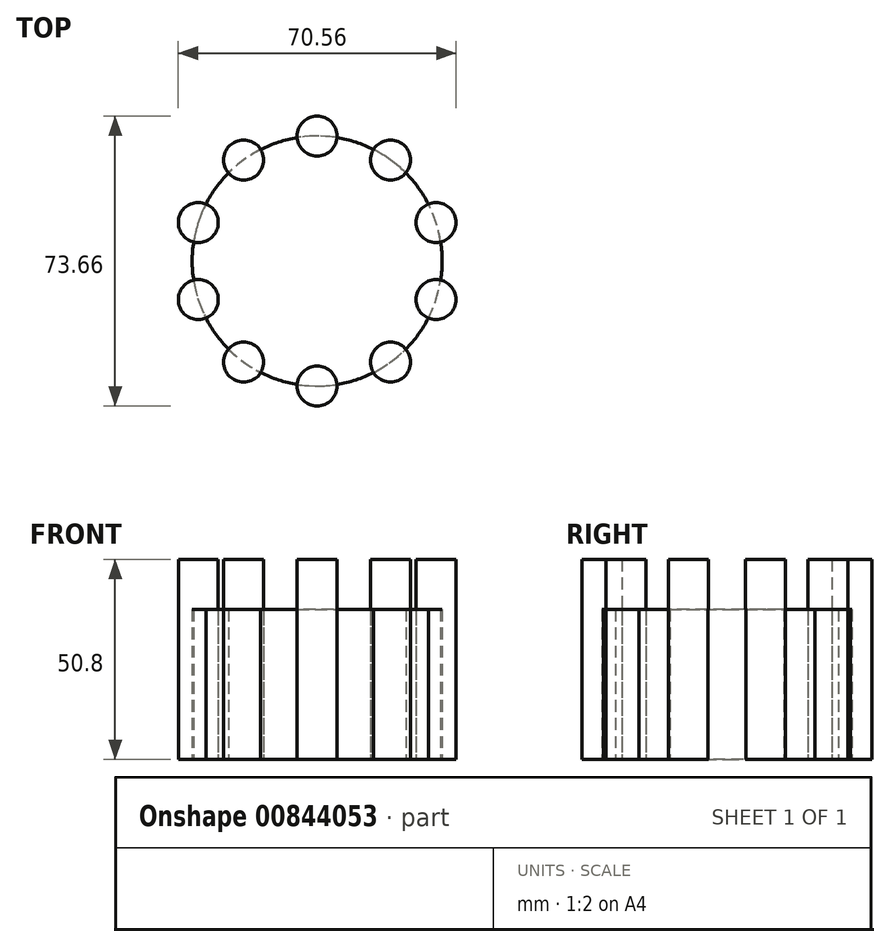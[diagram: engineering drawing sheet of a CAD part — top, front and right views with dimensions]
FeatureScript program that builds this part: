
annotation { "Feature Type Name" : "Feature", "Feature Type Description" : "" }
export const myFeature = defineFeature(function(context is Context, id is Id, definition is map)
    precondition{}
    {
        {
            var Q0;
            Q0=qCreatedBy(makeId("Top.planeOp"),FACE);
            var sketch = newSketch(context, id + "F0", { "sketchPlane" : qUnion([Q0])});
            skCircle(sketch, "E0", {"center": v(0, 0) * mm, "radius": 31.75 * mm});
            skSolve(sketch);
        }
        {
            var Q0;
            Q0=qSketchRegion(id+"F0",true);
            extrude(context, id + "F1", {"entities" : qUnion([Q0]), "depth" : 38.1 * mm});
        }
        {
            var Q0;
            Q0=qCreatedBy(makeId("Top.planeOp"),FACE);
            var sketch = newSketch(context, id + "F2", { "sketchPlane" : qUnion([Q0])});
            skCircle(sketch, "E1", {"center": v(0, 31.75) * mm, "radius": 5.08 * mm});
            skCircle(sketch, "E2.1.0", {"center": v(-18.66, 25.69) * mm, "radius": 5.08 * mm});
            skCircle(sketch, "E2.2.0", {"center": v(-30.2, 9.81) * mm, "radius": 5.08 * mm});
            skCircle(sketch, "E2.3.0", {"center": v(-30.2, -9.81) * mm, "radius": 5.08 * mm});
            skCircle(sketch, "E2.4.0", {"center": v(-18.66, -25.69) * mm, "radius": 5.08 * mm});
            skCircle(sketch, "E2.5.0", {"center": v(0, -31.75) * mm, "radius": 5.08 * mm});
            skCircle(sketch, "E2.6.0", {"center": v(18.66, -25.69) * mm, "radius": 5.08 * mm});
            skCircle(sketch, "E2.7.0", {"center": v(30.2, -9.81) * mm, "radius": 5.08 * mm});
            skCircle(sketch, "E2.8.0", {"center": v(30.2, 9.81) * mm, "radius": 5.08 * mm});
            skCircle(sketch, "E2.9.0", {"center": v(18.66, 25.69) * mm, "radius": 5.08 * mm});
            skPoint(sketch, "E2.center", {"position": v(0, 0) * mm});
            skSolve(sketch);
        }
        {
            var Q0;
            Q0=qSketchRegion(id+"F2",true);
            extrude(context, id + "F3", {"entities" : qUnion([Q0]), "depth" : 50.8 * mm});
        }
        {
            var Q0;
            Q0=makeQuery(id+"F3.opExtrude","SWEPT_BODY",BODY,{"disambiguationData":[OSD([sQuery(id+"F2.wireOp",EDGE,"E2.4.0")])]});
            var Q1;
            Q1=makeQuery(id+"F1.opExtrude","SWEPT_BODY",BODY,{"disambiguationData":[OSD([sQuery(id+"F0.wireOp",EDGE,"E0")])]});
            booleanBodies(context, id + "F4", {"operationType" : BooleanOperationType.INTERSECTION, "tools" : qUnion([Q0, Q1]), "keepTools" : true});
        }
        {
            var Q0;
            Q0=makeQuery(id+"F3.opExtrude","SWEPT_BODY",BODY,{"disambiguationData":[OSD([sQuery(id+"F2.wireOp",EDGE,"E2.3.0")])]});
            var Q1;
            Q1=makeQuery(id+"F1.opExtrude","SWEPT_BODY",BODY,{"disambiguationData":[OSD([sQuery(id+"F0.wireOp",EDGE,"E0")])]});
            booleanBodies(context, id + "F5", {"operationType" : BooleanOperationType.INTERSECTION, "tools" : qUnion([Q0, Q1]), "keepTools" : true});
        }
        {
            var Q0;
            Q0=makeQuery(id+"F3.opExtrude","SWEPT_BODY",BODY,{"disambiguationData":[OSD([sQuery(id+"F2.wireOp",EDGE,"E2.2.0")])]});
            var Q1;
            Q1=makeQuery(id+"F1.opExtrude","SWEPT_BODY",BODY,{"disambiguationData":[OSD([sQuery(id+"F0.wireOp",EDGE,"E0")])]});
            booleanBodies(context, id + "F6", {"operationType" : BooleanOperationType.INTERSECTION, "tools" : qUnion([Q0, Q1]), "keepTools" : true});
        }
        {
            var Q0;
            Q0=makeQuery(id+"F3.opExtrude","SWEPT_BODY",BODY,{"disambiguationData":[OSD([sQuery(id+"F2.wireOp",EDGE,"E2.1.0")])]});
            var Q1;
            Q1=makeQuery(id+"F1.opExtrude","SWEPT_BODY",BODY,{"disambiguationData":[OSD([sQuery(id+"F0.wireOp",EDGE,"E0")])]});
            booleanBodies(context, id + "F7", {"operationType" : BooleanOperationType.INTERSECTION, "tools" : qUnion([Q0, Q1]), "keepTools" : true});
        }
        {
            var Q0;
            Q0=makeQuery(id+"F3.opExtrude","SWEPT_BODY",BODY,{"disambiguationData":[OSD([sQuery(id+"F2.wireOp",EDGE,"E1")])]});
            var Q1;
            Q1=makeQuery(id+"F1.opExtrude","SWEPT_BODY",BODY,{"disambiguationData":[OSD([sQuery(id+"F0.wireOp",EDGE,"E0")])]});
            booleanBodies(context, id + "F8", {"operationType" : BooleanOperationType.INTERSECTION, "tools" : qUnion([Q0, Q1]), "keepTools" : true});
        }
        {
            var Q0;
            Q0=makeQuery(id+"F3.opExtrude","SWEPT_BODY",BODY,{"disambiguationData":[OSD([sQuery(id+"F2.wireOp",EDGE,"E2.9.0")])]});
            var Q1;
            Q1=makeQuery(id+"F1.opExtrude","SWEPT_BODY",BODY,{"disambiguationData":[OSD([sQuery(id+"F0.wireOp",EDGE,"E0")])]});
            booleanBodies(context, id + "F9", {"operationType" : BooleanOperationType.INTERSECTION, "tools" : qUnion([Q0, Q1]), "keepTools" : true});
        }
        {
            var Q0;
            Q0=makeQuery(id+"F1.opExtrude","SWEPT_BODY",BODY,{"disambiguationData":[OSD([sQuery(id+"F0.wireOp",EDGE,"E0")])]});
            var Q1;
            Q1=makeQuery(id+"F3.opExtrude","SWEPT_BODY",BODY,{"disambiguationData":[OSD([sQuery(id+"F2.wireOp",EDGE,"E2.8.0")])]});
            booleanBodies(context, id + "F10", {"operationType" : BooleanOperationType.INTERSECTION, "tools" : qUnion([Q0, Q1]), "keepTools" : true});
        }
        {
            var Q0;
            Q0=makeQuery(id+"F1.opExtrude","SWEPT_BODY",BODY,{"disambiguationData":[OSD([sQuery(id+"F0.wireOp",EDGE,"E0")])]});
            var Q1;
            Q1=makeQuery(id+"F3.opExtrude","SWEPT_BODY",BODY,{"disambiguationData":[OSD([sQuery(id+"F2.wireOp",EDGE,"E2.7.0")])]});
            booleanBodies(context, id + "F11", {"operationType" : BooleanOperationType.INTERSECTION, "tools" : qUnion([Q0, Q1]), "keepTools" : true});
        }
        {
            var Q0;
            Q0=makeQuery(id+"F1.opExtrude","SWEPT_BODY",BODY,{"disambiguationData":[OSD([sQuery(id+"F0.wireOp",EDGE,"E0")])]});
            var Q1;
            Q1=makeQuery(id+"F3.opExtrude","SWEPT_BODY",BODY,{"disambiguationData":[OSD([sQuery(id+"F2.wireOp",EDGE,"E2.6.0")])]});
            booleanBodies(context, id + "F12", {"operationType" : BooleanOperationType.INTERSECTION, "tools" : qUnion([Q0, Q1]), "keepTools" : true});
        }
        {
            var Q0;
            Q0=makeQuery(id+"F1.opExtrude","SWEPT_BODY",BODY,{"disambiguationData":[OSD([sQuery(id+"F0.wireOp",EDGE,"E0")])]});
            var Q1;
            Q1=makeQuery(id+"F3.opExtrude","SWEPT_BODY",BODY,{"disambiguationData":[OSD([sQuery(id+"F2.wireOp",EDGE,"E2.5.0")])]});
            booleanBodies(context, id + "F13", {"operationType" : BooleanOperationType.INTERSECTION, "tools" : qUnion([Q0, Q1]), "keepTools" : true});
        }
    });
